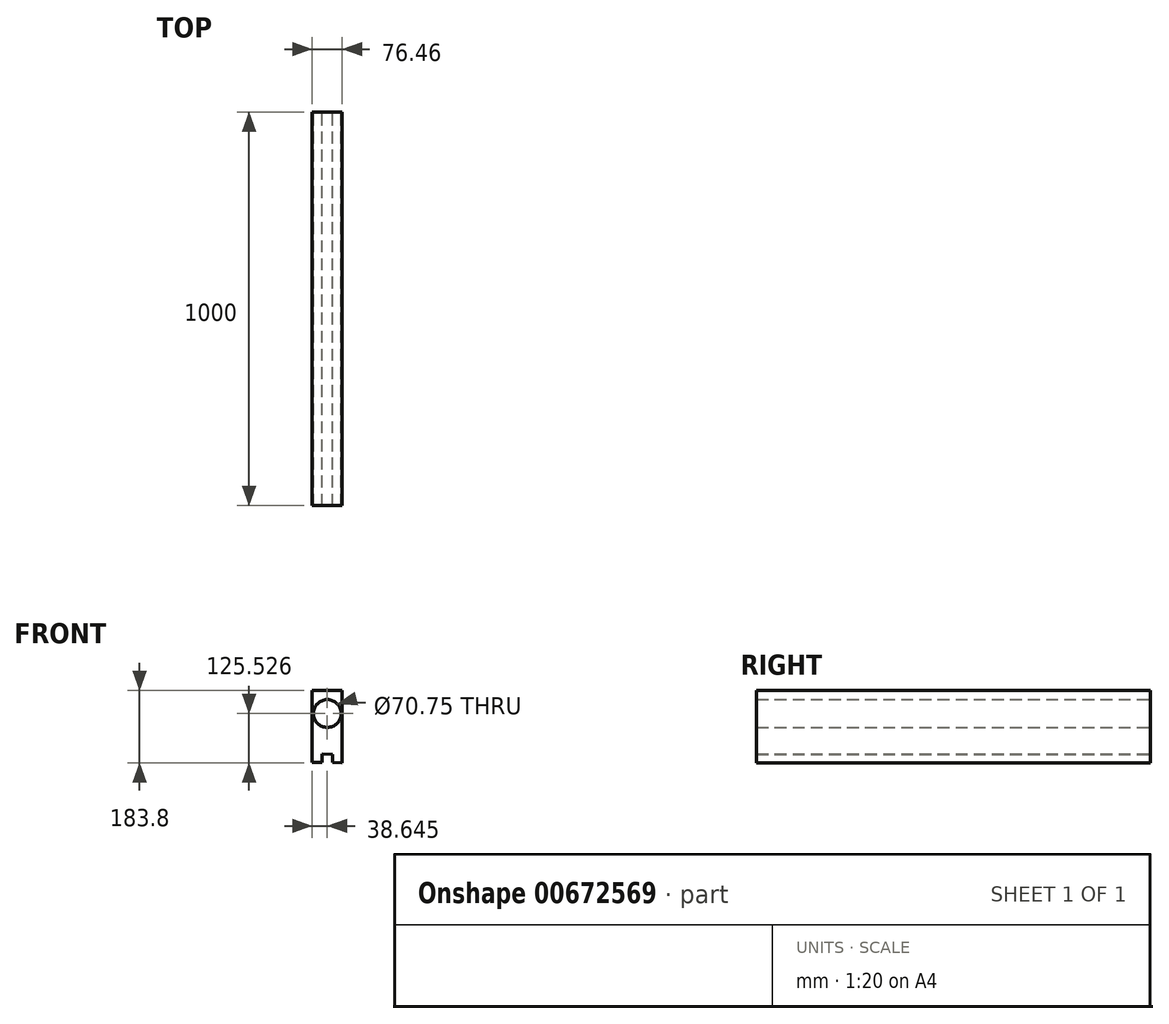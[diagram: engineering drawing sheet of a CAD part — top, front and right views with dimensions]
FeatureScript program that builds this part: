
annotation { "Feature Type Name" : "Feature", "Feature Type Description" : "" }
export const myFeature = defineFeature(function(context is Context, id is Id, definition is map)
    precondition{}
    {
        {
            var Q0;
            Q0=qCreatedBy(makeId("Front.planeOp"),FACE);
            var sketch = newSketch(context, id + "F0", { "sketchPlane" : qUnion([Q0])});
            skLineSegment(sketch, "E0.bottom", {"start": v(38.23, 57.95) * mm, "end": v(-38.23, 57.95) * mm});
            skLineSegment(sketch, "E0.top", {"start": v(38.23, -57.95) * mm, "end": v(-38.23, -57.95) * mm});
            skLineSegment(sketch, "E0.left", {"start": v(38.23, 57.95) * mm, "end": v(38.23, -57.95) * mm});
            skLineSegment(sketch, "E0.right", {"start": v(-38.23, 57.95) * mm, "end": v(-38.23, -57.95) * mm});
            skPoint(sketch, "E0.middle", {"position": v(0, 0) * mm});
            skCircle(sketch, "E1", {"center": v(0.42, -0.32) * mm, "radius": 35.38 * mm});
            skLineSegment(sketch, "E2", {"start": v(-38.23, -57.95) * mm, "end": v(-38.23, -124.75) * mm});
            skLineSegment(sketch, "E3", {"start": v(-38.23, -124.75) * mm, "end": v(-13.31, -124.75) * mm});
            skLineSegment(sketch, "E4", {"start": v(38.23, -57.95) * mm, "end": v(38.23, -125.85) * mm});
            skLineSegment(sketch, "E5", {"start": v(38.23, -125.85) * mm, "end": v(14.13, -124.89) * mm});
            skLineSegment(sketch, "E6", {"start": v(-13.31, -124.75) * mm, "end": v(-13.31, -103.5) * mm});
            skLineSegment(sketch, "E7", {"start": v(14.13, -124.89) * mm, "end": v(14.13, -104.13) * mm});
            skLineSegment(sketch, "E8", {"start": v(14.13, -104.13) * mm, "end": v(-13.31, -103.5) * mm});
            skSolve(sketch);
        }
        {
            var Q0;
            Q0 = qSketchRegion(id + "F0", true);
            extrude(context, id + "F1", {"entities" : qUnion([Q0]), "depth" : 1000 * mm, "offsetDistance" : 25.4 * mm});
        }
        {
            var Q0;
            Q0 = qSketchRegion(id + "F0", true);
            extrude(context, id + "F2", {"entities" : qUnion([Q0]), "operationType" : NewBodyOperationType.ADD, "depth" : 600 * mm, "offsetDistance" : 25.4 * mm});
        }
    });
